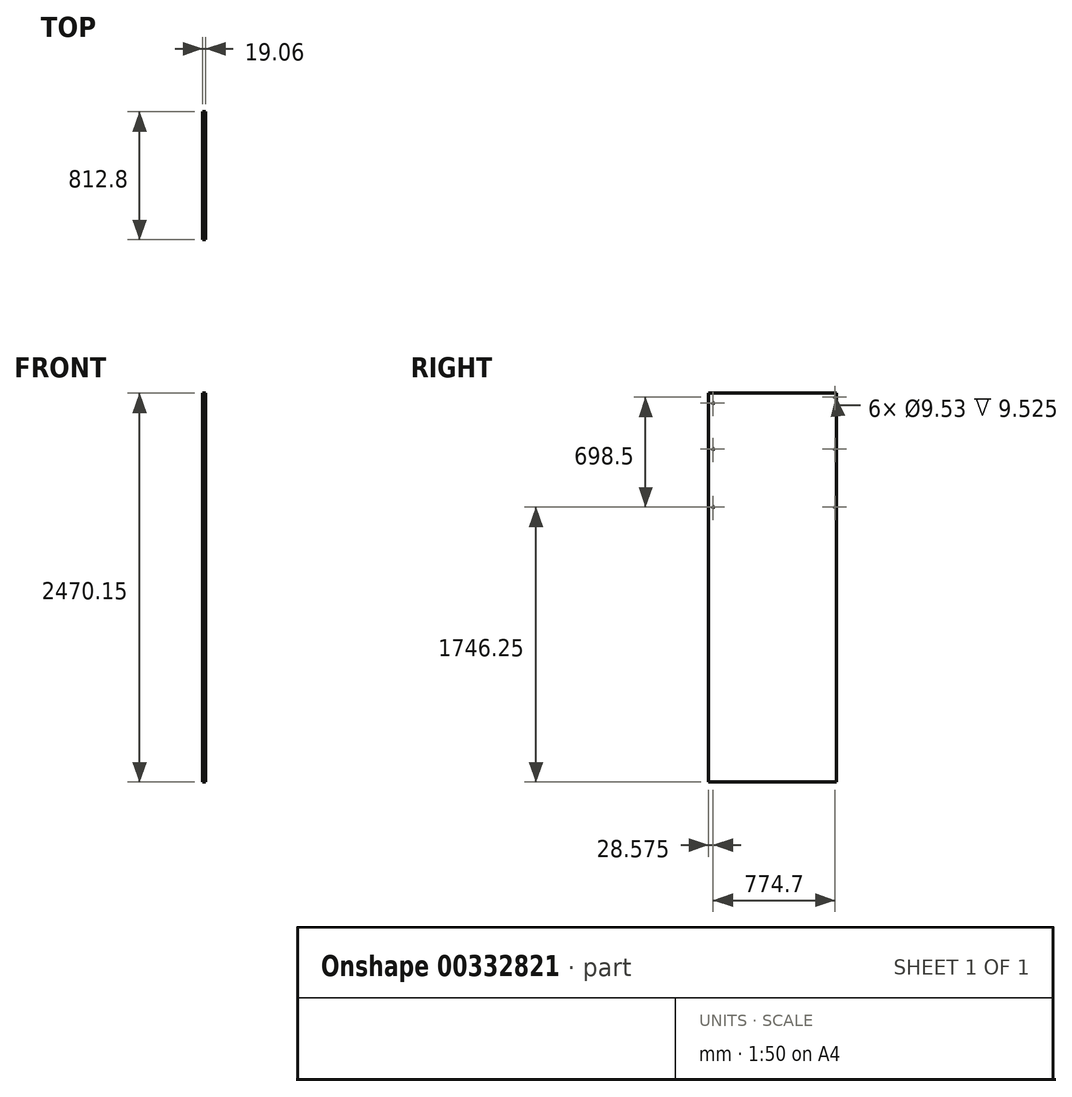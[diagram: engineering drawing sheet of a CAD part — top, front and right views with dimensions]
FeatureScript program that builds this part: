
annotation { "Feature Type Name" : "Feature", "Feature Type Description" : "" }
export const myFeature = defineFeature(function(context is Context, id is Id, definition is map)
    precondition{}
    {
        {
            var Q0;
            Q0=qCreatedBy(makeId("Right.planeOp"),FACE);
            var sketch = newSketch(context, id + "F0", { "sketchPlane" : qUnion([Q0])});
            skLineSegment(sketch, "E0.bottom", {"start": v(0, 0) * mm, "end": v(-812.8, 0) * mm});
            skLineSegment(sketch, "E0.top", {"start": v(0, 2470.15) * mm, "end": v(-812.8, 2470.15) * mm});
            skLineSegment(sketch, "E0.left", {"start": v(0, 0) * mm, "end": v(0, 2470.15) * mm});
            skLineSegment(sketch, "E0.right", {"start": v(-812.8, 0) * mm, "end": v(-812.8, 2470.15) * mm});
            skSolve(sketch);
        }
        {
            var Q0;
            Q0=qSketchRegion(id+"F0",true);
            extrude(context, id + "F1", {"entities" : qUnion([Q0]), "endBound" : BoundingType.SYMMETRIC, "depth" : 19.05 * mm});
        }
        {
            var Q0;
            Q0=qCreatedBy(makeId("Right.planeOp"),FACE);
            var sketch = newSketch(context, id + "F2", { "sketchPlane" : qUnion([Q0])});
            skCircle(sketch, "E1", {"center": v(-784.23, 2114.55) * mm, "radius": 4.76 * mm});
            skCircle(sketch, "E2", {"center": v(-784.23, 2406.65) * mm, "radius": 4.76 * mm});
            skCircle(sketch, "E3", {"center": v(-9.53, 2444.75) * mm, "radius": 4.76 * mm});
            skCircle(sketch, "E4", {"center": v(-9.53, 2114.55) * mm, "radius": 4.76 * mm});
            skCircle(sketch, "E5", {"center": v(-784.23, 1746.25) * mm, "radius": 4.76 * mm});
            skCircle(sketch, "E6", {"center": v(-9.53, 1746.25) * mm, "radius": 4.76 * mm});
            skSolve(sketch);
        }
        {
            var Q0;
            Q0=qSketchRegion(id+"F2",true);
            extrude(context, id + "F3", {"entities" : qUnion([Q0]), "operationType" : NewBodyOperationType.REMOVE, "depth" : 19.05 * mm});
        }
    });
